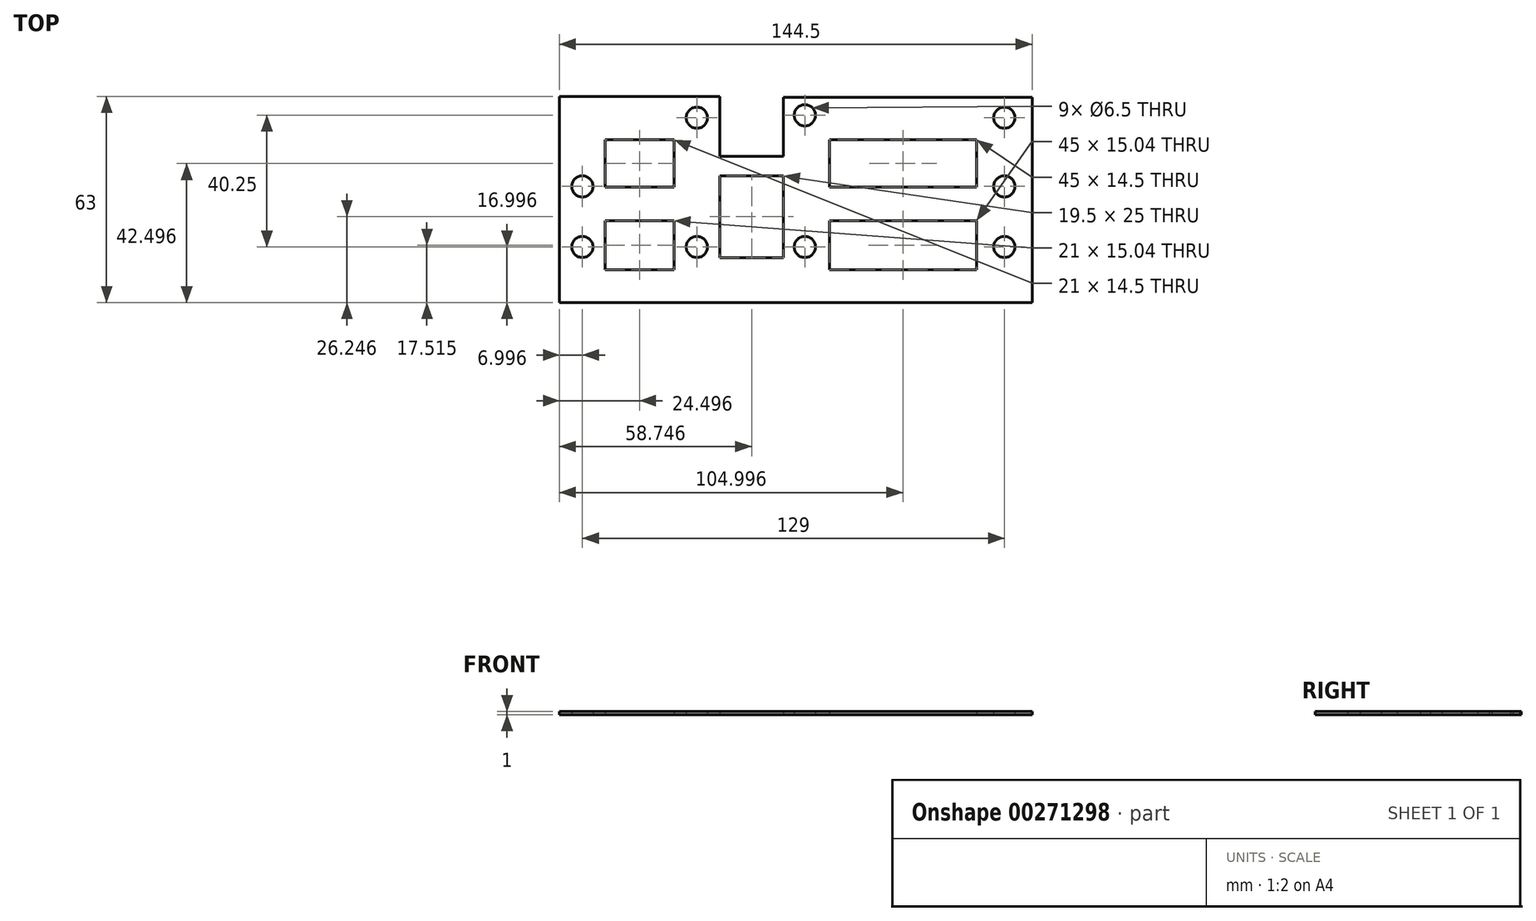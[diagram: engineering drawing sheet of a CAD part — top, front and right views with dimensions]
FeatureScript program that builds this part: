
annotation { "Feature Type Name" : "Feature", "Feature Type Description" : "" }
export const myFeature = defineFeature(function(context is Context, id is Id, definition is map)
    precondition{}
    {
        {
            var Q0;
            Q0=qCreatedBy(makeId("Top.planeOp"),FACE);
            var sketch = newSketch(context, id + "F0", { "sketchPlane" : qUnion([Q0])});
            skLineSegment(sketch, "E0.right", {"start": v(85.27, 26.29) * mm, "end": v(85.27, 13.29) * mm});
            skLineSegment(sketch, "E1.left", {"start": v(-24.23, 13.29) * mm, "end": v(-24.23, -26.46) * mm});
            skLineSegment(sketch, "E1.right", {"start": v(-10.23, 13.29) * mm, "end": v(-10.23, -26.46) * mm});
            skLineSegment(sketch, "E2.right", {"start": v(23.27, 13.29) * mm, "end": v(23.27, -26.46) * mm});
            skLineSegment(sketch, "E3.left", {"start": v(68.27, 13.29) * mm, "end": v(68.27, -26.46) * mm});
            skLineSegment(sketch, "E3.right", {"start": v(85.27, 13.29) * mm, "end": v(85.27, -26.46) * mm});
            skLineSegment(sketch, "E4", {"start": v(23.27, -11.43) * mm, "end": v(68.27, -11.43) * mm});
            skLineSegment(sketch, "E5", {"start": v(-24.23, -36.46) * mm, "end": v(85.27, -36.46) * mm});
            skLineSegment(sketch, "E6", {"start": v(85.27, -26.46) * mm, "end": v(85.27, -36.46) * mm});
            skLineSegment(sketch, "E7", {"start": v(-10.23, 2.29) * mm, "end": v(9.27, 2.29) * mm});
            skLineSegment(sketch, "E8", {"start": v(23.27, -1.21) * mm, "end": v(68.27, -1.21) * mm});
            skLineSegment(sketch, "E9", {"start": v(-59.23, -26.46) * mm, "end": v(-59.23, -36.46) * mm});
            skLineSegment(sketch, "E10", {"start": v(-59.23, -36.46) * mm, "end": v(-24.23, -36.46) * mm});
            skCircle(sketch, "E11", {"center": v(-17.23, 20.04) * mm, "radius": 3.25 * mm});
            skLineSegment(sketch, "E12", {"start": v(23.27, 13.29) * mm, "end": v(68.27, 13.29) * mm});
            skLineSegment(sketch, "E13", {"start": v(-59.23, 26.54) * mm, "end": v(-59.23, -26.46) * mm});
            skLineSegment(sketch, "E14", {"start": v(-24.23, 13.29) * mm, "end": v(-45.23, 13.29) * mm});
            skLineSegment(sketch, "E15", {"start": v(-45.23, 13.29) * mm, "end": v(-45.23, -26.46) * mm});
            skLineSegment(sketch, "E16", {"start": v(-10.23, -22.71) * mm, "end": v(9.27, -22.71) * mm});
            skCircle(sketch, "E17", {"center": v(-52.23, -19.46) * mm, "radius": 3.25 * mm});
            skCircle(sketch, "E18", {"center": v(-52.23, -0.96) * mm, "radius": 3.25 * mm});
            skLineSegment(sketch, "E19", {"start": v(-24.23, -11.43) * mm, "end": v(-45.23, -11.43) * mm});
            skPoint(sketch, "E19.startSnap0", {"position": v(-24.23, -6.59) * mm});
            skLineSegment(sketch, "E20", {"start": v(-24.23, -1.21) * mm, "end": v(-45.23, -1.21) * mm});
            skLineSegment(sketch, "E21", {"start": v(-24.23, -26.46) * mm, "end": v(-10.23, -26.46) * mm});
            skLineSegment(sketch, "E22", {"start": v(9.27, -26.46) * mm, "end": v(68.27, -26.46) * mm});
            skLineSegment(sketch, "E23", {"start": v(-24.23, -26.46) * mm, "end": v(-45.23, -26.46) * mm});
            skLineSegment(sketch, "E24", {"start": v(-45.23, 13.29) * mm, "end": v(-59.23, 13.29) * mm});
            skLineSegment(sketch, "E25", {"start": v(-24.23, 13.29) * mm, "end": v(-10.23, 13.29) * mm});
            skLineSegment(sketch, "E26", {"start": v(68.27, 13.29) * mm, "end": v(85.27, 13.29) * mm});
            skLineSegment(sketch, "E27", {"start": v(-59.23, 26.54) * mm, "end": v(-10.23, 26.54) * mm});
            skLineSegment(sketch, "E28", {"start": v(-10.23, 26.54) * mm, "end": v(-10.23, 13.29) * mm});
            skLineSegment(sketch, "E29", {"start": v(85.27, 26.29) * mm, "end": v(9.27, 26.29) * mm});
            skLineSegment(sketch, "E30", {"start": v(-10.23, 8.27) * mm, "end": v(9.27, 8.27) * mm});
            skCircle(sketch, "E31", {"center": v(76.77, 20.04) * mm, "radius": 3.25 * mm});
            skCircle(sketch, "E32", {"center": v(15.77, 20.79) * mm, "radius": 3.25 * mm});
            skCircle(sketch, "E33", {"center": v(76.77, -0.96) * mm, "radius": 3.25 * mm});
            skCircle(sketch, "E34", {"center": v(76.77, -19.46) * mm, "radius": 3.25 * mm});
            skCircle(sketch, "E35", {"center": v(-17.23, -19.46) * mm, "radius": 3.25 * mm});
            skPoint(sketch, "E35.centerSnap0", {"position": v(-17.23, 13.29) * mm});
            skCircle(sketch, "E36", {"center": v(15.77, -19.46) * mm, "radius": 3.25 * mm});
            skLineSegment(sketch, "E37", {"start": v(9.27, -26.46) * mm, "end": v(9.27, 8.27) * mm});
            skLineSegment(sketch, "E38", {"start": v(23.27, 13.29) * mm, "end": v(9.27, 13.29) * mm});
            skLineSegment(sketch, "E39", {"start": v(9.27, 13.29) * mm, "end": v(9.27, 8.27) * mm});
            skLineSegment(sketch, "E40", {"start": v(9.27, 13.29) * mm, "end": v(9.27, 26.29) * mm});
            skSolve(sketch);
        }
        {
            var Q0;
            Q0=makeQuery(id+"F0.imprint","IMPRINT",FACE,{"disambiguationData":[TD([[makeQuery(id+"F0.imprint","IMPRINT",EDGE,{"derivedFrom":sQuery(id+"F0.wireOp",EDGE,"E0.bottom")}),-1.0]])]});
            var Q1;
            Q1=makeQuery(id+"F0.imprint","IMPRINT",FACE,{"disambiguationData":[TD([[makeQuery(id+"F0.imprint","IMPRINT",EDGE,{"derivedFrom":sQuery(id+"F0.wireOp",EDGE,"E3.right")}),-1.0]])]});
            var Q2;
            {var subQ0=sQuery(id+"F0.wireOp",EDGE,"E19");Q2=makeQuery(id+"F0.imprint","IMPRINT",FACE,{"disambiguationData":[TD([[makeQuery(id+"F0.imprint","IMPRINT",EDGE,{"derivedFrom":subQ0}),-1.0]])]});}
            var Q3;
            Q3=makeQuery(id+"F0.imprint","IMPRINT",FACE,{"disambiguationData":[TD([[makeQuery(id+"F0.imprint","IMPRINT",EDGE,{"derivedFrom":sQuery(id+"F0.wireOp",EDGE,"9QRmkq9x-BRBA-see5-K7w2-NajFg8qcSFQK")}),-1.0]])]});
            var Q4;
            {var subQ2=sQuery(id+"F0.wireOp",EDGE,"E7");Q4=makeQuery(id+"F0.imprint","IMPRINT",FACE,{"disambiguationData":[TD([[makeQuery(id+"F0.imprint","IMPRINT",EDGE,{"derivedFrom":subQ2}),1.0]])]});}
            var Q5;
            Q5=makeQuery(id+"F0.imprint","IMPRINT",FACE,{"disambiguationData":[TD([[makeQuery(id+"F0.imprint","IMPRINT",EDGE,{"derivedFrom":sQuery(id+"F0.wireOp",EDGE,"7Detu8iB-xN4Y-ylVN-SToU-Ujbpg4SeMbeG")}),-1.0]])]});
            var Q6;
            {var subQ0=sQuery(id+"F0.wireOp",EDGE,"E4");Q6=makeQuery(id+"F0.imprint","IMPRINT",FACE,{"disambiguationData":[TD([[makeQuery(id+"F0.imprint","IMPRINT",EDGE,{"derivedFrom":subQ0}),1.0]])]});}
            var Q7;
            Q7=makeQuery(id+"F0.imprint","IMPRINT",FACE,{"disambiguationData":[TD([[makeQuery(id+"F0.imprint","IMPRINT",EDGE,{"derivedFrom":sQuery(id+"F0.wireOp",EDGE,"E11")}),-1.0]])]});
            var Q8;
            Q8=makeQuery(id+"F0.imprint","IMPRINT",FACE,{"disambiguationData":[TD([[makeQuery(id+"F0.imprint","IMPRINT",EDGE,{"derivedFrom":sQuery(id+"F0.wireOp",EDGE,"E0.right")}),-1.0]])]});
            var Q9;
            {var subQ3=sQuery(id+"F0.wireOp",EDGE,"E21");Q9=makeQuery(id+"F0.imprint","IMPRINT",FACE,{"disambiguationData":[TD([[makeQuery(id+"F0.imprint","IMPRINT",EDGE,{"derivedFrom":subQ3}),1.0]])]});}
            var Q10;
            Q10=makeQuery(id+"F0.imprint","IMPRINT",FACE,{"disambiguationData":[TD([[makeQuery(id+"F0.imprint","IMPRINT",EDGE,{"derivedFrom":sQuery(id+"F0.wireOp",EDGE,"E36")}),-1.0]])]});
            extrude(context, id + "F1", {"entities" : qUnion([Q0, Q1, Q2, Q3, Q4, Q5, Q6, Q7, Q8, Q9, Q10]), "depth" : 1 * mm});
        }
    });
